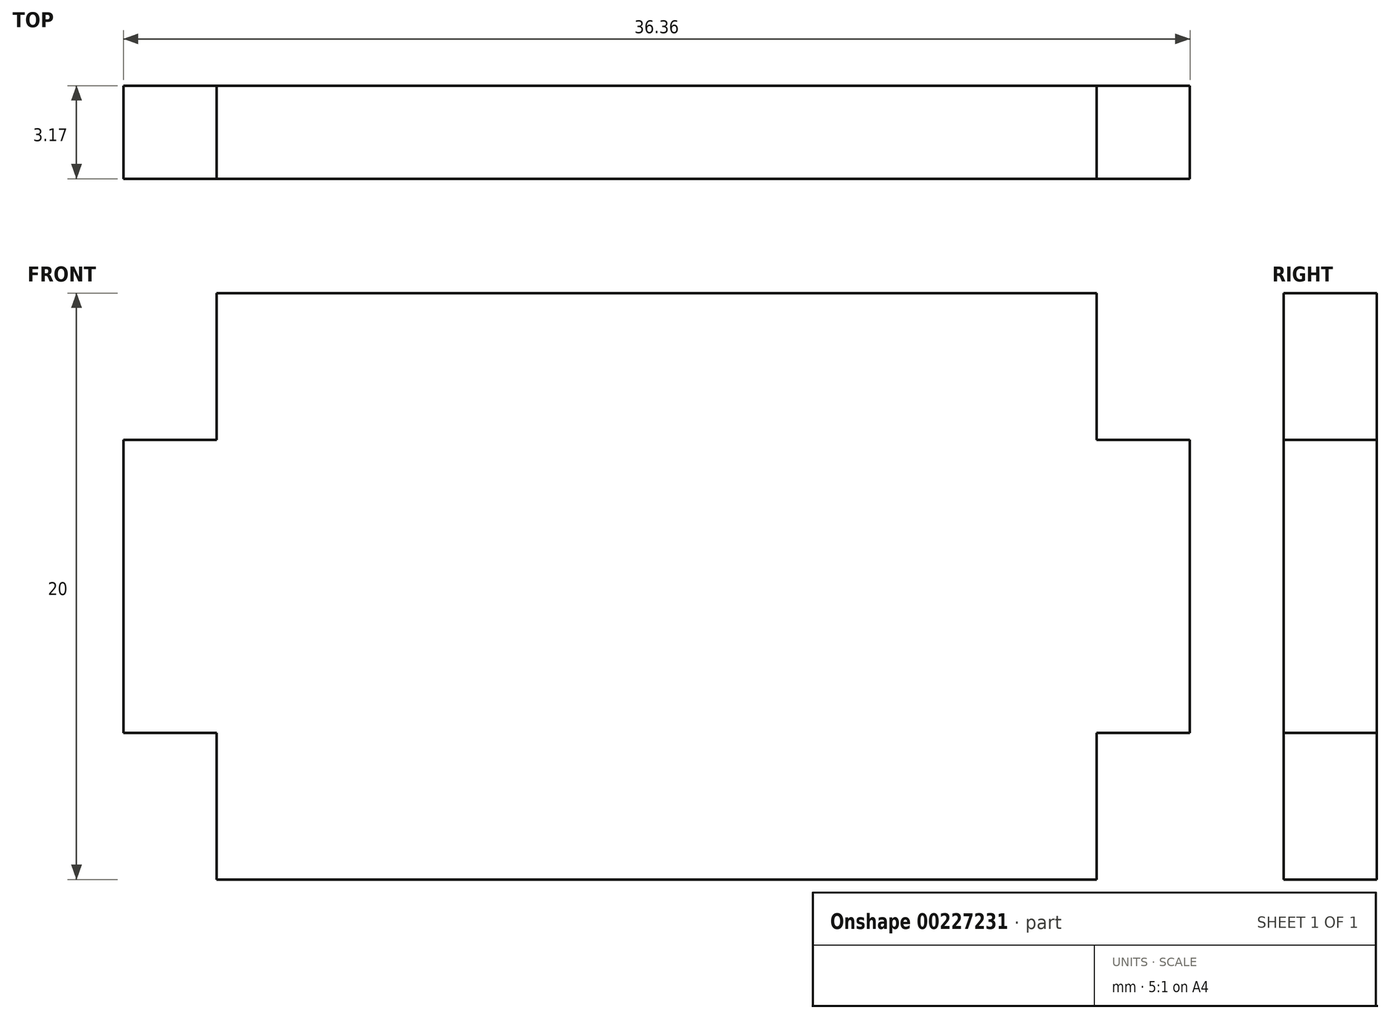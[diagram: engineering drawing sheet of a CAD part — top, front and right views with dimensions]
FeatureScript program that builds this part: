
annotation { "Feature Type Name" : "Feature", "Feature Type Description" : "" }
export const myFeature = defineFeature(function(context is Context, id is Id, definition is map)
    precondition{}
    {
        {
            var Q0;
            Q0=qCreatedBy(makeId("Front.planeOp"),FACE);
            var sketch = newSketch(context, id + "F0", { "sketchPlane" : qUnion([Q0])});
            skLineSegment(sketch, "E0.bottom", {"start": v(18.18, -5) * mm, "end": v(-18.18, -5) * mm});
            skLineSegment(sketch, "E0.top", {"start": v(18.18, 5) * mm, "end": v(-18.18, 5) * mm});
            skLineSegment(sketch, "E0.left", {"start": v(18.17, -5) * mm, "end": v(18.17, 5) * mm});
            skLineSegment(sketch, "E0.right", {"start": v(-18.18, -5) * mm, "end": v(-18.18, 5) * mm});
            skPoint(sketch, "E0.middle", {"position": v(0, 0) * mm});
            skLineSegment(sketch, "E1", {"start": v(-15, 5) * mm, "end": v(-15, 10) * mm});
            skLineSegment(sketch, "E2", {"start": v(-15, 10) * mm, "end": v(15, 10) * mm});
            skLineSegment(sketch, "E3", {"start": v(15, 10) * mm, "end": v(15, 5) * mm});
            skLineSegment(sketch, "E4.MirrorCS", {"start": v(-15, -5) * mm, "end": v(-15, -10) * mm});
            skLineSegment(sketch, "E5.MirrorCS", {"start": v(-15, -10) * mm, "end": v(15, -10) * mm});
            skLineSegment(sketch, "E6.MirrorCS", {"start": v(15, -10) * mm, "end": v(15, -5) * mm});
            skSolve(sketch);
        }
        {
            var Q0;
            Q0 = qSketchRegion(id + "F0", true);
            extrude(context, id + "F1", {"entities" : qUnion([Q0]), "depth" : 3.17 * mm});
        }
    });
